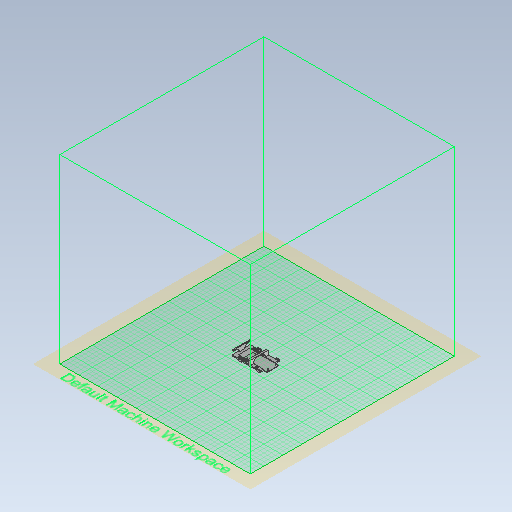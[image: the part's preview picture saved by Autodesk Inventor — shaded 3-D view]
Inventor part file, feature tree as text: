
AUTODESK INVENTOR PART (.ipt)
format: ipt  version: 2021 (Build 250183000, 183)  size: 1,754,624 bytes
history: native  units: in
note: dims shown in document units (in); Inventor stores cm internally (conversion verified against a paired STEP export)
features: extrude x12, sketch x11, fillet x6, mirror x3, plane x2, chamfer x1
ambient origin geometry x8: Origin, YZ Plane, XZ Plane, XY Plane, X Axis, Y Axis, Z Axis, Center Point
bodies: Solid1 (feature_tree)
feature tree (35):
  extrude  "Extrusion1"  Depth=0.7756in
  extrude  "Extrusion2"  Depth=0.2362in
  plane  "Work Plane1"
  extrude  "Extrusion3"  Depth=0.2362in
  sketch  "Sketch5"  dims[d14=1.3386in d15=0.0in]
  extrude  "Extrusion4"  TaperAngle=0.0deg  [1 undecoded]
  sketch  "Sketch7"  dims[d19=0.8661in d20=0.374in d21=0.0in d22=0.7756in]
  extrude  "Extrusion5"  Depth=0.1575in
  plane  "Work Plane2"
  extrude  "Extrusion8"  Depth=0.374in
  fillet  "Fillet3"  [1 undecoded]
  fillet  "Fillet4"  Radius=0.7756in
  sketch  "Sketch13"  dims[d26=1.4803in]
  extrude  "Extrusion9"  Depth=0.5in
  mirror  "Mirror3"
  chamfer  "Chamfer1"  Distance=0.748in
  extrude  "Extrusion11"  Depth=0.5in
  extrude  "Extrusion13"  Depth=0.0472in TaperAngle=0.0deg
  mirror  "Mirror4"
  extrude  "Extrusion14"  Depth=0.0787in
  extrude  "Extrusion15"  Depth=0.2756in
  mirror  "Mirror5"
  fillet  "Fillet8"  Radius=0.0709in
  fillet  "Fillet9"  Radius=0.0945in
  fillet  "Fillet10"  Radius=1.8in
  extrude  "Extrusion17"  Depth=0.35in
  fillet  "Fillet11"  Radius=0.1575in
  sketch  "Sketch1"  dims[d5=2.4409in d6=0.7756in]
  sketch  "Sketch3"  dims[d7=0.0945in d8=0.0in d9=0.2362in]
  sketch  "Sketch4"  dims[d10=0.0787in d11=0.0in d13=0.2362in]
  sketch  "Sketch6"  dims[d16=0.063in d17=0.0in d18=0.1575in]
  sketch  "Sketch8"  dims[d23=0.374in d24=0.5in]
  sketch  "Sketch12"  dims[d25=0.315in]
  sketch  "Sketch18"  dims[d27=0.0in d29=-0.748in d30=0.748in]
  sketch  "Sketch19"  dims[d41=1.785in d42=0.5in d43=0.0472in d44=0.0in d46=0.0787in d47=0.2756in d48=0.0709in d49=0.0945in d50=1.8in d51=0.35in d52=0.1575in d53=0.0in d56=0.5512in d57=0.0472in d58=45.0deg d59=0.0787in d60=0.0787in d61=0.0394in d64=0.0394in d66=0.0787in d67=0.0394in d68=0.0in d69=0.0in d70=0.0in d71=0.2397in d72=0.2397in d74=0.315in d76=0.2362in d77=0.0787in d78=0.0in d79=0.0945in d84=0.2953in d85=0.0in d86=0.0in d87=0.0787in d90=0.0787in d91=0.7756in d92=0.0787in d93=0.0in d96=0.0in d97=0.2362in d98=0.2756in d99=0.0787in d100=0.0in d101=0.315in d104=0.0472in d105=0.0472in d106=0.5118in d107=0.0in d108=0.5118in d102=0.0197in d103=0.0344in]
note: 2 required parameter values undecoded (feature->parameter linkage not recoverable at this tier; creation-order binding heuristic only, values carry confidence <= 0.55)
